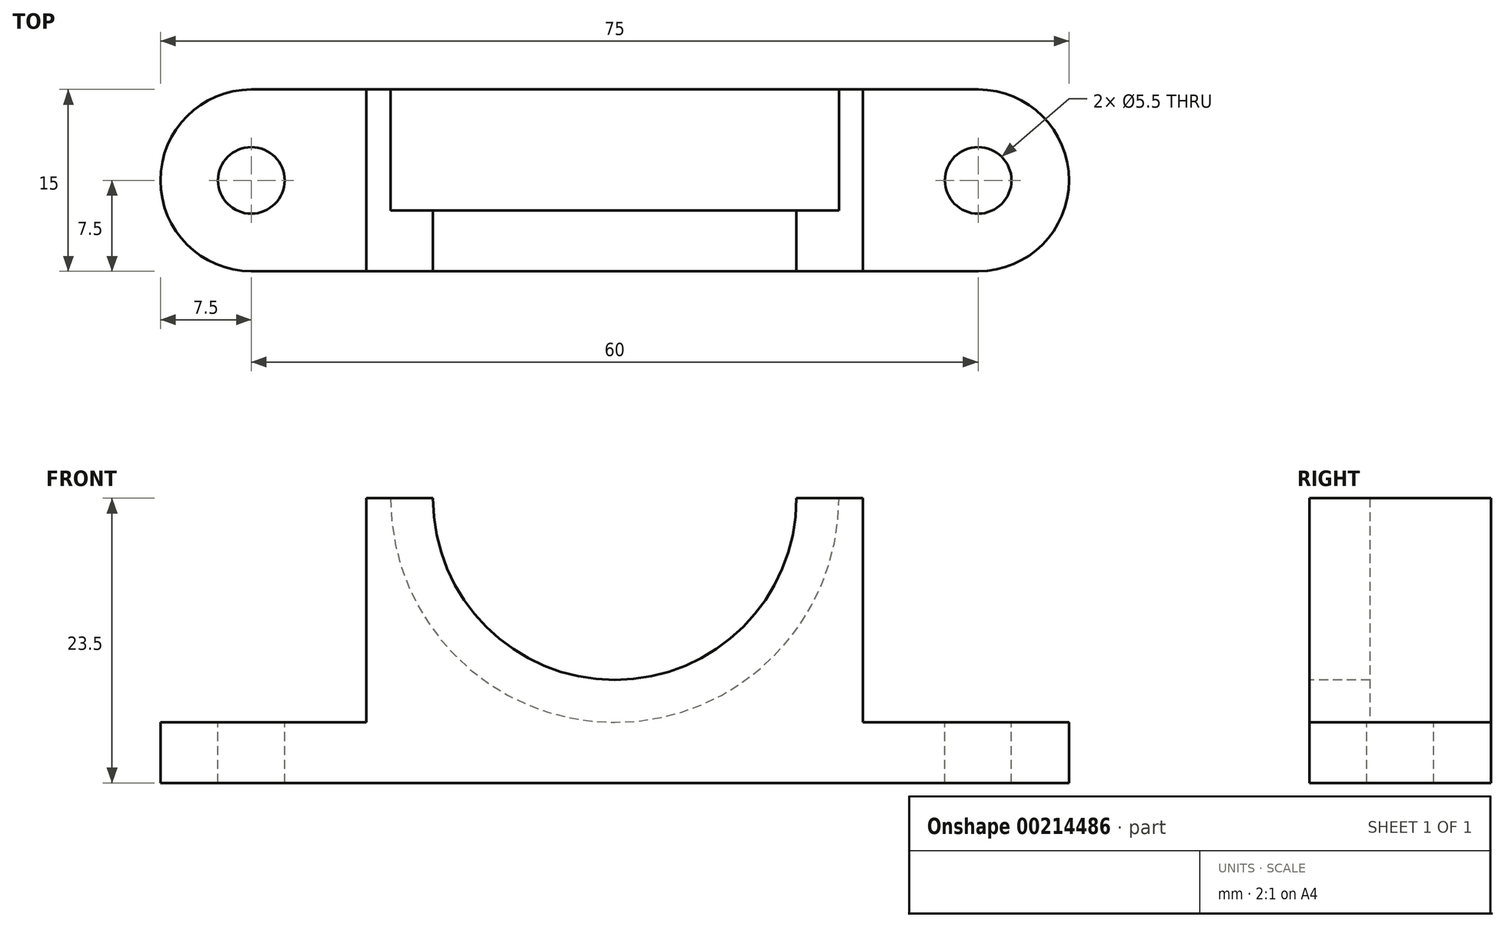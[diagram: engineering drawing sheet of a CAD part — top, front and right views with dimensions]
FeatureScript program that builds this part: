
annotation { "Feature Type Name" : "Feature", "Feature Type Description" : "" }
export const myFeature = defineFeature(function(context is Context, id is Id, definition is map)
    precondition{}
    {
        {
            var Q0;
            Q0=qCreatedBy(makeId("Top.planeOp"),FACE);
            var sketch = newSketch(context, id + "F0", { "sketchPlane" : qUnion([Q0])});
            skLineSegment(sketch, "E0.bottom", {"start": v(-30, 7.5) * mm, "end": v(30, 7.5) * mm});
            skLineSegment(sketch, "E0.top", {"start": v(-30, -7.5) * mm, "end": v(30, -7.5) * mm});
            skLineSegment(sketch, "E0.left", {"start": v(-30, 7.5) * mm, "end": v(-30, -7.5) * mm});
            skLineSegment(sketch, "E0.right", {"start": v(30, 7.5) * mm, "end": v(30, -7.5) * mm});
            skPoint(sketch, "E0.middle", {"position": v(0, 0) * mm});
            skArc(sketch, "E1", {"start": v(-30, 7.5) * mm, "mid": v(-37.5, 0) * mm, "end": v(-30, -7.5) * mm});
            skArc(sketch, "E2", {"start": v(30, 7.5) * mm, "mid": v(37.5, 0) * mm, "end": v(30, -7.5) * mm});
            skSolve(sketch);
        }
        {
            var Q0;
            Q0=qSketchRegion(id+"F0",true);
            extrude(context, id + "F1", {"entities" : qUnion([Q0]), "depth" : 5 * mm});
        }
        {
            var Q0;
            Q0=makeQuery(id+"F1.opExtrude","SWEPT_FACE",FACE,{"disambiguationData":[OSD([sQuery(id+"F0.wireOp",EDGE,"E0.top")])]});
            var sketch = newSketch(context, id + "F2", { "sketchPlane" : qUnion([Q0])});
            skCircle(sketch, "E3", {"center": v(0, 23.5) * mm, "radius": 18.5 * mm});
            skPoint(sketch, "E3.centerSnap0", {"position": v(0, 0) * mm});
            skCircle(sketch, "E4", {"center": v(0, 23.5) * mm, "radius": 20.5 * mm});
            skLineSegment(sketch, "E5", {"start": v(-20.5, 23.5) * mm, "end": v(-20.5, 5) * mm});
            skLineSegment(sketch, "E6", {"start": v(0, 23.5) * mm, "end": v(0, 0) * mm, "construction": true});
            skLineSegment(sketch, "E7.MirrorCS", {"start": v(20.5, 23.5) * mm, "end": v(20.5, 5) * mm});
            skLineSegment(sketch, "E8", {"start": v(-20.5, 23.5) * mm, "end": v(-15, 23.5) * mm});
            skLineSegment(sketch, "E9", {"start": v(20.5, 23.5) * mm, "end": v(15, 23.5) * mm});
            skCircle(sketch, "E10", {"center": v(0, 23.5) * mm, "radius": 15 * mm});
            skSolve(sketch);
        }
        {
            var Q0;
            {var subQ0=sQuery(id+"F2.wireOp",EDGE,"E5");Q0=makeQuery(id+"F2.imprint","IMPRINT",FACE,{"disambiguationData":[TD([[makeQuery(id+"F2.imprint","IMPRINT",EDGE,{"derivedFrom":subQ0}),1.0]])]});}
            var Q1;
            {var subQ0=sQuery(id+"F2.wireOp",EDGE,"E8");Q1=makeQuery(id+"F2.imprint","IMPRINT",FACE,{"disambiguationData":[TD([[makeQuery(id+"F2.imprint","IMPRINT",EDGE,{"derivedFrom":subQ0}),-1.0]])]});}
            var Q2;
            {var subQ0=sQuery(id+"F2.wireOp",EDGE,"E9");Q2=makeQuery(id+"F2.imprint","IMPRINT",FACE,{"disambiguationData":[TD([[makeQuery(id+"F2.imprint","IMPRINT",EDGE,{"derivedFrom":subQ0}),1.0]])]});}
            var Q3;
            {var subQ0=sQuery(id+"F2.wireOp",EDGE,"E7.MirrorCS");Q3=makeQuery(id+"F2.imprint","IMPRINT",FACE,{"disambiguationData":[TD([[makeQuery(id+"F2.imprint","IMPRINT",EDGE,{"derivedFrom":subQ0}),-1.0]])]});}
            extrude(context, id + "F3", {"entities" : qUnion([Q0, Q1, Q2, Q3]), "operationType" : NewBodyOperationType.ADD, "oppositeDirection" : true, "depth" : 15 * mm});
        }
        {
            var Q0;
            {var subQ1=sQuery(id+"F2.wireOp",EDGE,"E8");var subQ3=sQuery(id+"F2.wireOp",EDGE,"E3");var subQ4=makeQuery(id+"F2.imprint","INTERSECT",VERTEX,{"derivedFrom":[subQ3,subQ1]});Q0=makeQuery(id+"F2.imprint","IMPRINT",FACE,{"disambiguationData":[TD([[makeQuery(id+"F2.imprint","IMPRINT",EDGE,{"disambiguationData":[TD([[subQ4,-1.0]])],"derivedFrom":subQ3}),1.0]])]});}
            extrude(context, id + "F4", {"entities" : qUnion([Q0]), "operationType" : NewBodyOperationType.ADD, "oppositeDirection" : true, "depth" : 5 * mm});
        }
        {
            var Q0;
            {var subQ3=sQuery(id+"F0.wireOp",EDGE,"E0.top");var subQ4=sQuery(id+"F0.wireOp",EDGE,"E2");var subQ5=sQuery(id+"F0.wireOp",EDGE,"E0.bottom");Q0=makeQuery(id+"F3.boolean.opBoolean","SPLIT",FACE,{"disambiguationData":[TD([makeQuery(id+"F1.opExtrude","SWEPT_FACE",FACE,{"disambiguationData":[OSD([subQ4])]})])],"derivedFrom":makeQuery(id+"F1.opExtrude","CAP_FACE",FACE,{"disambiguationData":[OSD([subQ5,subQ3,sQuery(id+"F0.wireOp",EDGE,"E1"),subQ4])],"isStart":false})});}
            var sketch = newSketch(context, id + "F5", { "sketchPlane" : qUnion([Q0])});
            skPoint(sketch, "E11", {"position": v(-30, 0) * mm});
            skPoint(sketch, "E12", {"position": v(30, 0) * mm});
            skSolve(sketch);
        }
        {
            var Q0;
            Q0=sQuery(id+"F5.wireOp",VERTEX,"E12");
            var Q1;
            Q1=sQuery(id+"F5.wireOp",VERTEX,"E11");
            var Q2;
            Q2=makeQuery(id+"F1.opExtrude","SWEPT_BODY",BODY,{"disambiguationData":[OSD([sQuery(id+"F0.wireOp",EDGE,"E0.bottom"),sQuery(id+"F0.wireOp",EDGE,"E0.top"),sQuery(id+"F0.wireOp",EDGE,"E1"),sQuery(id+"F0.wireOp",EDGE,"E2")])]});
            hole(context, id + "F6", {"style" : HoleStyle.SIMPLE, "endStyle" : HoleEndStyle.THROUGH, "standardTappedOrClearance" : lookupTablePath({ "standard" : "ISO", "fit" : "Normal", "size" : "M5", "type" : "Clearance" }), "standardBlindInLast" : lookupTablePath({ "fit" : "Standard", "standard" : "ISO", "size" : "M5", "type" : "Clearance" }), "holeDiameter" : 5.5 * mm, "locations" : qUnion([Q0, Q1]), "scope" : qUnion([Q2]), "isTappedThrough" : true});
        }
    });
